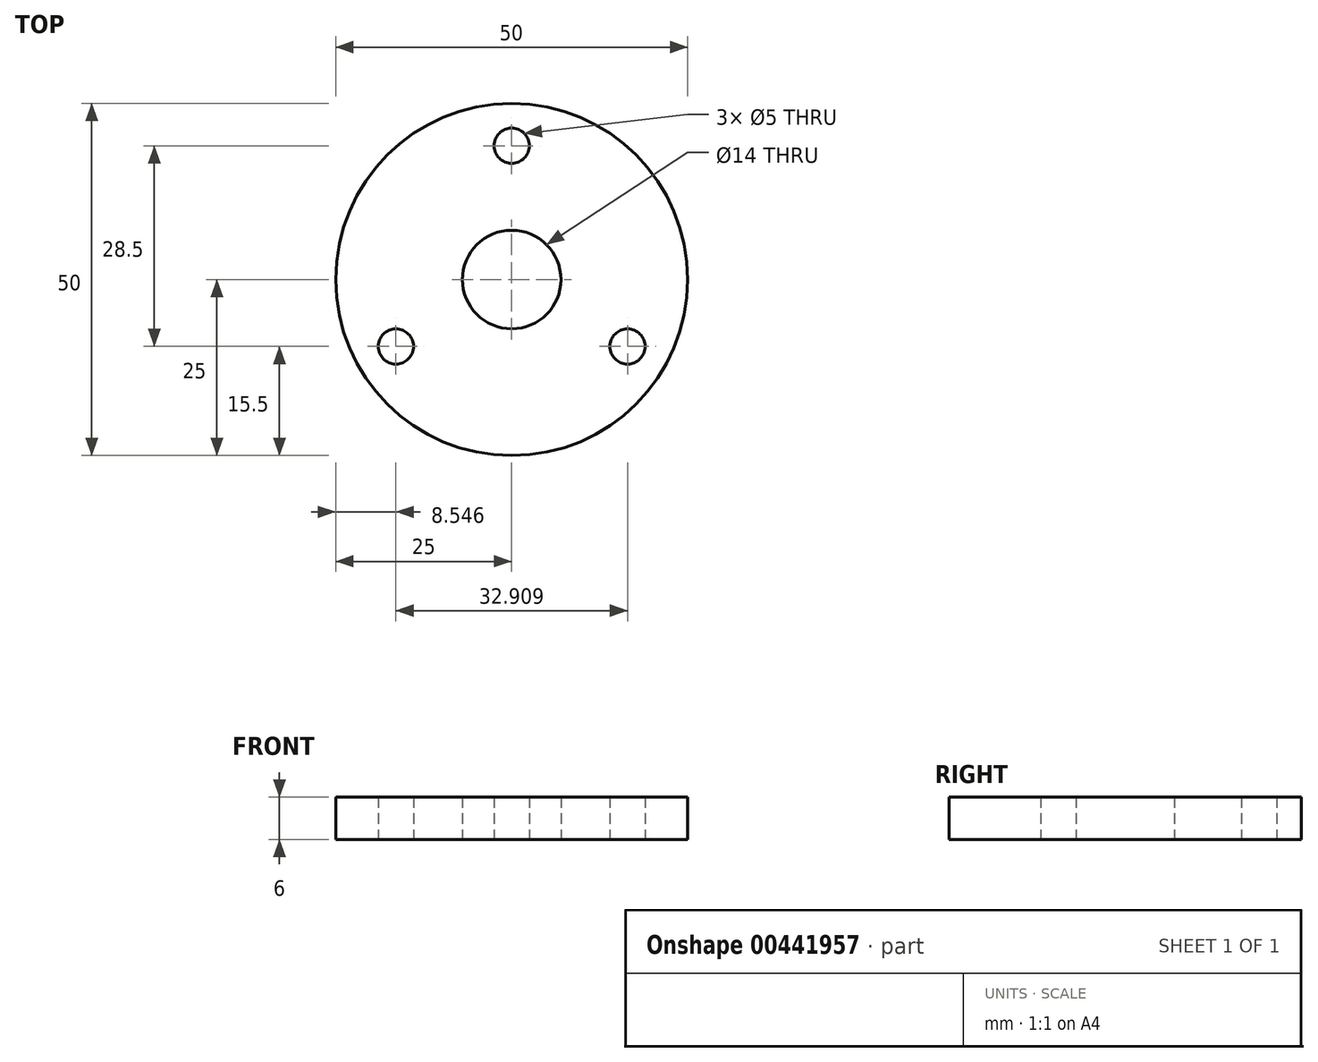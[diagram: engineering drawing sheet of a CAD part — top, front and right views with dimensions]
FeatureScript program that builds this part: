
annotation { "Feature Type Name" : "Feature", "Feature Type Description" : "" }
export const myFeature = defineFeature(function(context is Context, id is Id, definition is map)
    precondition{}
    {
        {
            var Q0;
            Q0=qCreatedBy(makeId("Top.planeOp"),FACE);
            var sketch = newSketch(context, id + "F0", { "sketchPlane" : qUnion([Q0])});
            skCircle(sketch, "E0", {"center": v(0, 0) * mm, "radius": 7 * mm});
            skCircle(sketch, "E1", {"center": v(0, 0) * mm, "radius": 25 * mm});
            skSolve(sketch);
        }
        {
            var Q0;
            Q0=qCreatedBy(makeId("Top.planeOp"),FACE);
            var sketch = newSketch(context, id + "F1", { "sketchPlane" : qUnion([Q0])});
            skCircle(sketch, "E2", {"center": v(16.45, -9.5) * mm, "radius": 2.5 * mm});
            skCircle(sketch, "E3", {"center": v(0, 19) * mm, "radius": 2.5 * mm});
            skCircle(sketch, "E4", {"center": v(-16.45, -9.5) * mm, "radius": 2.5 * mm});
            skSolve(sketch);
        }
        {
            var Q0;
            Q0=makeQuery(id+"F0.imprint","IMPRINT",FACE,{"disambiguationData":[TD([[makeQuery(id+"F0.imprint","IMPRINT",EDGE,{"derivedFrom":sQuery(id+"F0.wireOp",EDGE,"E0")}),-1.0]])]});
            extrude(context, id + "F2", {"entities" : qUnion([Q0]), "depth" : 6 * mm, "offsetDistance" : 25 * mm});
        }
        {
            var Q0;
            Q0 = qSketchRegion(id + "F1", true);
            extrude(context, id + "F3", {"entities" : qUnion([Q0]), "operationType" : NewBodyOperationType.REMOVE, "oppositeDirection" : true, "depth" : -6 * mm, "offsetDistance" : 25 * mm});
        }
    });
